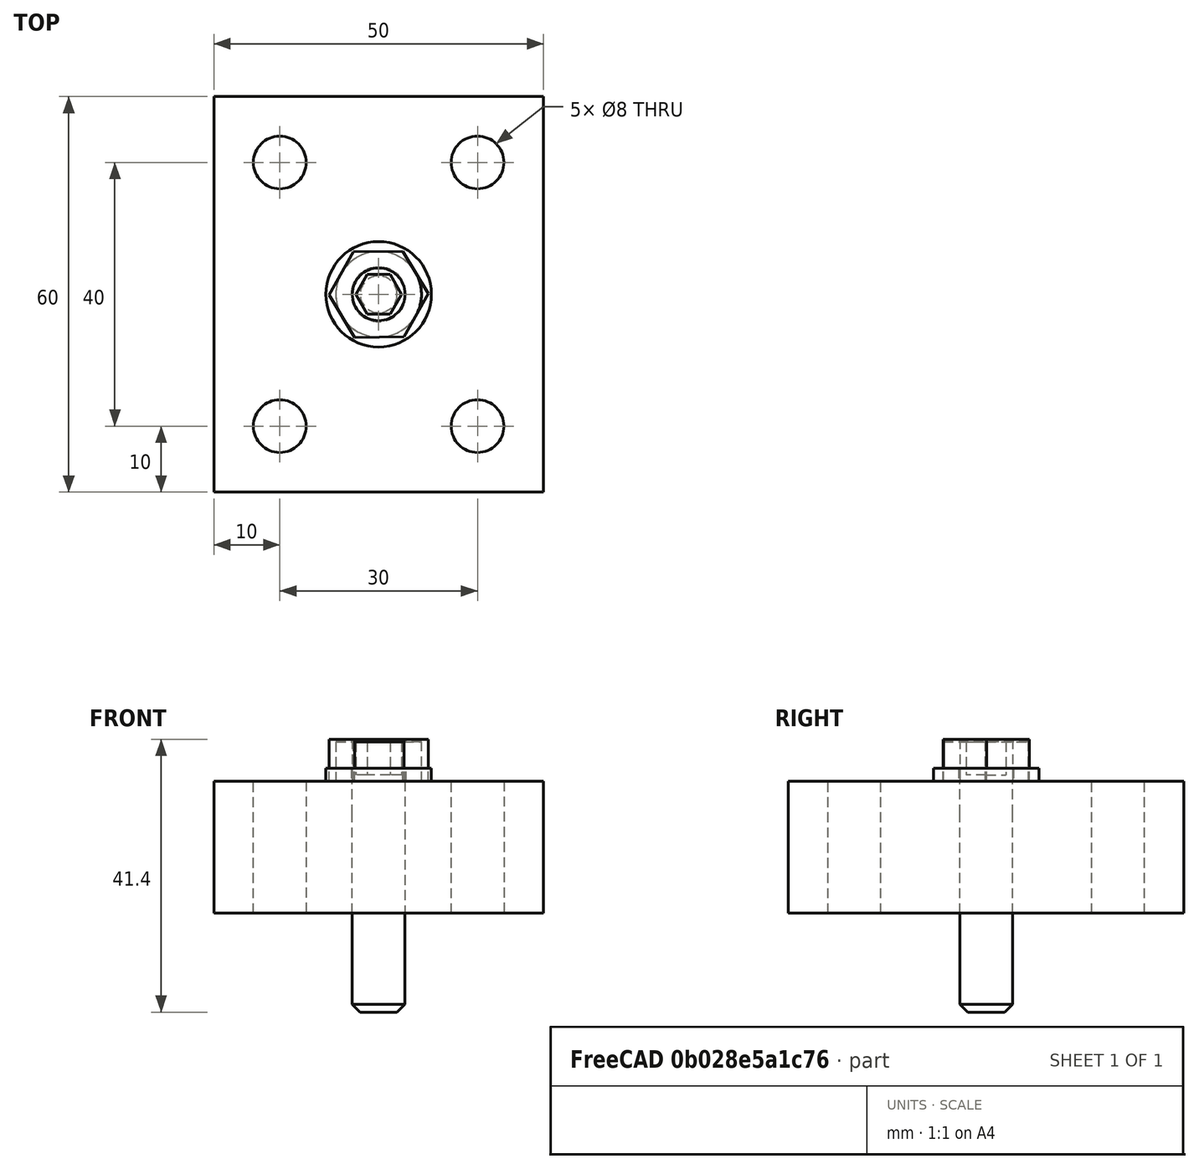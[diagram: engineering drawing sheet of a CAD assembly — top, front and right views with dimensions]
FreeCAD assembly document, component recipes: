
FREECAD ASSEMBLY — COMPONENT RECIPES ("asm3-basics-3-011")

This assembly document has 4 components, labeled P0..P3 below (a component is one placed body or linked part). 4 of them carry a construction recipe — the FreeCAD feature program that regenerates the part from scratch, quoted from this document or its linked companion documents; the rest are supplied as boundary geometry only. No exploded tour is included for this assembly.
COMPONENT P0 — recipe-attached ("Body", modeled in this document).
Construction recipe (the document's own serialized feature program — sketch geometry with constraints, then the solid features built on it; lengths are millimeters unless a unit is written):

FEATURE [Sketcher::SketchObject] Sketch
  MapMode = 5
  Support = -> [XY_Plane]
  sketch-geometry (2):
    g0: Circle CenterX=0 CenterY=0 CenterZ=0 NormalX=0 NormalY=0 NormalZ=1 AngleXU=0 Radius=4.15
    g1: Circle CenterX=0 CenterY=0 CenterZ=0 NormalX=0 NormalY=0 NormalZ=1 AngleXU=0 Radius=8
  constraints (4):
    c: Coincident(g0,g-1)
    c: Coincident(g1,g0)
    c: Diameter(g0) = 8.3  'D1'
    c: Diameter(g1) = 16  'D2'
FEATURE [PartDesign::Pad] Pad
  ClaimChildren = false
  Length = 2
  Length2 = 100
  Profile = -> Sketch
  Type = 0
FEATURE [PartDesign::Body] Body
  Group = -> [Sketch,Pad]
  Origin = -> Origin
  Tip = -> Pad
COMPONENT P1 — recipe-attached ("Body001", modeled in this document).
Construction recipe (the document's own serialized feature program — sketch geometry with constraints, then the solid features built on it; lengths are millimeters unless a unit is written):

FEATURE [Sketcher::SketchObject] Sketch001
  MapMode = 5
  Support = -> [XY_Plane001]
  sketch-geometry (8):
    g0: Circle CenterX=0 CenterY=0 CenterZ=0 NormalX=0 NormalY=0 NormalZ=1 AngleXU=0 Radius=4
    g1: LineSegment StartX=7.50496 StartY=0.0945881 StartZ=0 EndX=3.67056 EndY=6.54678 EndZ=0
    g2: LineSegment StartX=3.67056 StartY=6.54678 StartZ=0 EndX=-3.83439 EndY=6.45219 EndZ=0
    g3: LineSegment StartX=-3.83439 StartY=6.45219 StartZ=0 EndX=-7.50496 EndY=-0.0945881 EndZ=0
    g4: LineSegment StartX=-7.50496 StartY=-0.0945881 StartZ=0 EndX=-3.67056 EndY=-6.54678 EndZ=0
    g5: LineSegment StartX=-3.67056 StartY=-6.54678 StartZ=0 EndX=3.83439 EndY=-6.45219 EndZ=0
    g6: LineSegment StartX=3.83439 StartY=-6.45219 StartZ=0 EndX=7.50496 EndY=0.0945881 EndZ=0
    g7: Circle [constr] CenterX=0 CenterY=0 CenterZ=0 NormalX=0 NormalY=0 NormalZ=1 AngleXU=0 Radius=7.50555
  constraints (17):
    c: Coincident(g0,g-1)
    c: Diameter(g0) = 8  'D1'
    c: Coincident(g1,g2)
    c: Coincident(g2,g3)
    c: Coincident(g3,g4)
    c: Coincident(g4,g5)
    c: Coincident(g5,g6)
    c: Coincident(g6,g1)
    c: Equal(g1, g2-g6) x5
    c: PointOnObject(g1,g7)
    c: PointOnObject(g2,g7)
    c: PointOnObject(g3,g7)
    c: PointOnObject(g4,g7)
    c: PointOnObject(g5,g7)
    c: PointOnObject(g6,g7)
    c: Coincident(g7,g0)
    c: Distance(g1,g5) = 13  'WS'
FEATURE [PartDesign::Pad] Pad001
  ClaimChildren = false
  Length = 6.4
  Length2 = 100
  Profile = -> Sketch001
  Type = 0
FEATURE [PartDesign::Body] Body001
  Group = -> [Sketch001,Pad001]
  Origin = -> Origin001
  Tip = -> Pad001
COMPONENT P2 — recipe-attached ("Body002", modeled in this document).
Construction recipe (the document's own serialized feature program — sketch geometry with constraints, then the solid features built on it; lengths are millimeters unless a unit is written):

FEATURE [Sketcher::SketchObject] Sketch002
  MapMode = 5
  Support = -> [XY_Plane002]
  sketch-geometry (1):
    g0: Circle CenterX=0 CenterY=0 CenterZ=0 NormalX=0 NormalY=0 NormalZ=1 AngleXU=0 Radius=4
  constraints (2):
    c: Coincident(g0,g-1)
    c: Diameter(g0) = 8  'D1'
FEATURE [PartDesign::Pad] Pad002
  ClaimChildren = false
  Length = 5
  Length2 = 100
  Profile = -> Sketch002
  Reversed = true
  Type = 0
FEATURE [Sketcher::SketchObject] Sketch003
  ExternalGeometry = -> [Pad002]
  MapMode = 5
  Placement = pos=(0,0,-5) rot=(1,0,0;3.14159rad)
  Support = -> [Pad002]
FEATURE [PartDesign::Pad] Pad003
  BaseFeature = -> Pad002
  ClaimChildren = false
  Length = 30
  Length2 = 100
  Profile = -> Sketch003
  Type = 0
  expr: Length = Pad005.Length + 10mm
FEATURE [Sketcher::SketchObject] Sketch004
  MapMode = 5
  Support = -> [XY_Plane002]
  sketch-geometry (1):
    g0: Circle CenterX=0 CenterY=0 CenterZ=0 NormalX=0 NormalY=0 NormalZ=1 AngleXU=0 Radius=6.5
  constraints (2):
    c: Coincident(g0,g-1)
    c: Diameter(g0) = 13  'DH'
FEATURE [PartDesign::Pad] Pad004
  BaseFeature = -> Pad003
  ClaimChildren = false
  Length = 6
  Length2 = 100
  Profile = -> Sketch004
  Type = 0
FEATURE [Sketcher::SketchObject] Sketch005
  MapMode = 5
  Placement = pos=(0,0,6) rot=(0,0,1;0rad)
  Support = -> [Pad004]
  sketch-geometry (7):
    g0: LineSegment StartX=3.4641 StartY=0 StartZ=0 EndX=1.73205 EndY=3 EndZ=0
    g1: LineSegment StartX=1.73205 StartY=3 StartZ=0 EndX=-1.73205 EndY=3 EndZ=0
    g2: LineSegment StartX=-1.73205 StartY=3 StartZ=0 EndX=-3.4641 EndY=0 EndZ=0
    g3: LineSegment StartX=-3.4641 StartY=0 StartZ=0 EndX=-1.73205 EndY=-3 EndZ=0
    g4: LineSegment StartX=-1.73205 StartY=-3 StartZ=0 EndX=1.73205 EndY=-3 EndZ=0
    g5: LineSegment StartX=1.73205 StartY=-3 StartZ=0 EndX=3.4641 EndY=0 EndZ=0
    g6: Circle [constr] CenterX=0 CenterY=0 CenterZ=0 NormalX=0 NormalY=0 NormalZ=1 AngleXU=0 Radius=3.4641
  constraints (16):
    c: Coincident(g0,g1)
    c: Coincident(g1,g2)
    c: Coincident(g2,g3)
    c: Coincident(g3,g4)
    c: Coincident(g4,g5)
    c: Coincident(g5,g0)
    c: Equal(g0, g1-g5) x5
    c: PointOnObject(g0,g6)
    c: PointOnObject(g1,g6)
    c: PointOnObject(g2,g6)
    c: PointOnObject(g3,g6)
    c: PointOnObject(g4,g6)
    c: PointOnObject(g5,g6)
    c: Coincident(g6,g-1)
    c: PointOnObject(g5,g-1)
    c: Distance(g0,g4) = 6  'WS'
FEATURE [PartDesign::Pocket] Pocket
  BaseFeature = -> Pad004
  ClaimChildren = false
  Length = 5
  Length2 = 100
  Profile = -> Sketch005
  Type = 0
FEATURE [PartDesign::Chamfer] Chamfer
  Base = -> Pocket [Edge6]
  BaseFeature = -> Pocket
  Size = 1.2
FEATURE [PartDesign::Body] Body002
  Group = -> [Sketch002,Pad002,Sketch003,Pad003,Sketch004,Pad004,Sketch005,Pocket,Chamfer]
  Origin = -> Origin002
  Tip = -> Chamfer
COMPONENT P3 — recipe-attached ("Body003", modeled in this document).
Construction recipe (the document's own serialized feature program — sketch geometry with constraints, then the solid features built on it; lengths are millimeters unless a unit is written):

FEATURE [Sketcher::SketchObject] Sketch006
  MapMode = 5
  Support = -> [XY_Plane003]
  sketch-geometry (8):
    g0: Circle CenterX=-15 CenterY=20 CenterZ=0 NormalX=0 NormalY=0 NormalZ=1 AngleXU=0 Radius=4
    g1: Circle CenterX=15 CenterY=20 CenterZ=0 NormalX=0 NormalY=0 NormalZ=1 AngleXU=0 Radius=4
    g2: Circle CenterX=15 CenterY=-20 CenterZ=0 NormalX=0 NormalY=0 NormalZ=1 AngleXU=0 Radius=4
    g3: Circle CenterX=-15 CenterY=-20 CenterZ=0 NormalX=0 NormalY=0 NormalZ=1 AngleXU=0 Radius=4
    g4: LineSegment StartX=-25 StartY=30 StartZ=0 EndX=25 EndY=30 EndZ=0
    g5: LineSegment StartX=25 StartY=30 StartZ=0 EndX=25 EndY=-30 EndZ=0
    g6: LineSegment StartX=25 StartY=-30 StartZ=0 EndX=-25 EndY=-30 EndZ=0
    g7: LineSegment StartX=-25 StartY=-30 StartZ=0 EndX=-25 EndY=30 EndZ=0
  constraints (19):
    c: Equal(g0,g1)
    c: Equal(g1,g2)
    c: Equal(g2,g3)
    c: Diameter(g0) = 8  'BHD'
    c: Symmetric(g0,g1,g-2)
    c: Symmetric(g1,g2,g-1)
    c: Symmetric(g0,g3,g-1)
    c: Coincident(g4,g5)
    c: Coincident(g5,g6)
    c: Coincident(g6,g7)
    c: Coincident(g7,g4)
    c: Horizontal(g6)
    c: Vertical(g7)
    c: Symmetric(g4,g4,g-2)
    c: Symmetric(g4,g5,g-1)
    c: Distance(g3,g2) = 30  'L1'
    c: Distance(g4) = 50  'L2'
    c: Distance(g1,g2) = 40  'W1'
    c: Distance(g7) = 60  'W2'
FEATURE [PartDesign::Pad] Pad005
  ClaimChildren = false
  Length = 20
  Length2 = 100
  Profile = -> Sketch006
  Reversed = true
  Type = 0
FEATURE [PartDesign::Body] Body003
  Group = -> [Sketch006,Pad005]
  Origin = -> Origin003
  Tip = -> Pad005
PROVENANCE & LICENSES
A FreeCAD (.FCStd) document from a public repository crawl; recipes are the document's own serialized feature recipes (and, for linked parts, companion documents' recipes).
License: as declared in the source repository (recorded in the dataset sidecar).
